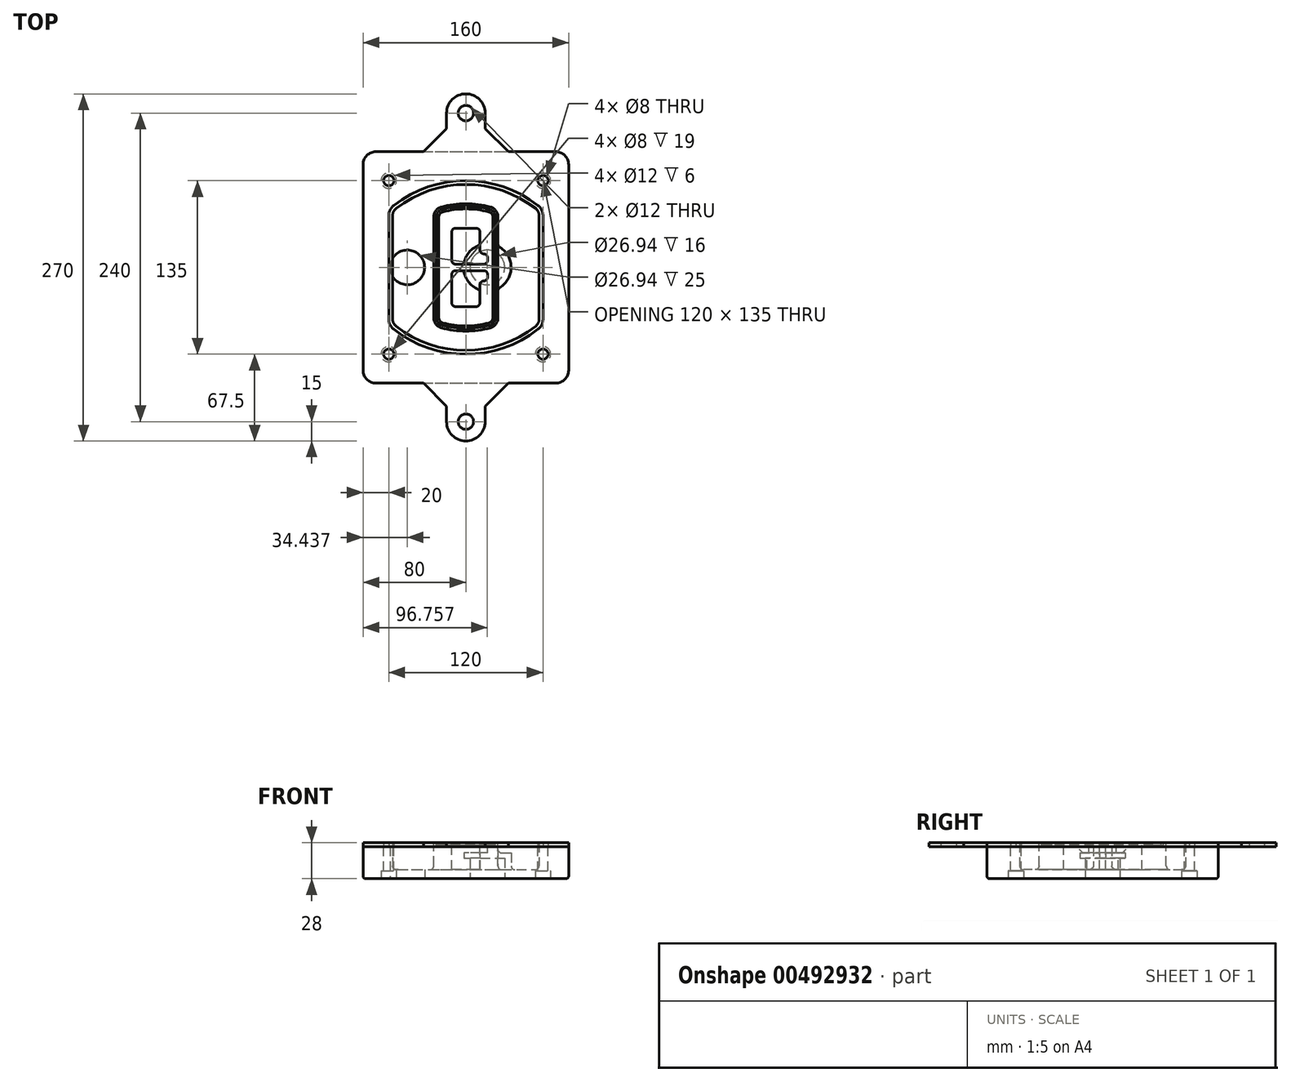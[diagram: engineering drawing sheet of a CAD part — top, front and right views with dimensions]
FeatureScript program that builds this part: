
annotation { "Feature Type Name" : "Feature", "Feature Type Description" : "" }
export const myFeature = defineFeature(function(context is Context, id is Id, definition is map)
    precondition{}
    {
        {
            var Q0;
            Q0=qCreatedBy(makeId("Top.planeOp"),FACE);
            var sketch = newSketch(context, id + "F0", { "sketchPlane" : qUnion([Q0])});
            skPoint(sketch, "E0.rect.middle", {"position": v(0, 0) * mm});
            skLineSegment(sketch, "E1.bottom", {"start": v(-70, -90) * mm, "end": v(70, -90) * mm});
            skLineSegment(sketch, "E1.top", {"start": v(-70, 90) * mm, "end": v(70, 90) * mm});
            skLineSegment(sketch, "E1.left", {"start": v(-80, -80) * mm, "end": v(-80, 80) * mm});
            skLineSegment(sketch, "E1.right", {"start": v(80, -80) * mm, "end": v(80, 80) * mm});
            skLineSegment(sketch, "E2", {"start": v(-80, 90) * mm, "end": v(80, -90) * mm, "construction": true});
            skLineSegment(sketch, "E3", {"start": v(80, 90) * mm, "end": v(-80, -90) * mm, "construction": true});
            skCircle(sketch, "E4", {"center": v(-60, 67.5) * mm, "radius": 4 * mm});
            skCircle(sketch, "E5", {"center": v(60, 67.5) * mm, "radius": 4 * mm});
            skCircle(sketch, "E6", {"center": v(60, -67.5) * mm, "radius": 4 * mm});
            skCircle(sketch, "E7", {"center": v(-60, -67.5) * mm, "radius": 4 * mm});
            skLineSegment(sketch, "E8", {"start": v(-60, 67.5) * mm, "end": v(60, 67.5) * mm, "construction": true});
            skLineSegment(sketch, "E9", {"start": v(60, 67.5) * mm, "end": v(60, -67.5) * mm, "construction": true});
            skLineSegment(sketch, "E10", {"start": v(60, -67.5) * mm, "end": v(-60, -67.5) * mm, "construction": true});
            skLineSegment(sketch, "E11", {"start": v(-60, -67.5) * mm, "end": v(-60, 67.5) * mm, "construction": true});
            skLineSegment(sketch, "E12", {"start": v(-60, 40.3) * mm, "end": v(-60, -40.3) * mm});
            skLineSegment(sketch, "E13", {"start": v(60, 40.3) * mm, "end": v(60, -40.3) * mm});
            skArc(sketch, "E14", {"start": v(56.15, 48.18) * mm, "mid": v(0, 67.5) * mm, "end": v(-56.15, 48.18) * mm});
            skArc(sketch, "E15", {"start": v(-56.15, -48.18) * mm, "mid": v(0, -67.5) * mm, "end": v(56.15, -48.18) * mm});
            skLineSegment(sketch, "E16", {"start": v(-60, 0) * mm, "end": v(60, 0) * mm, "construction": true});
            skPoint(sketch, "E17.visualSharp", {"position": v(-60, -45) * mm});
            skArc(sketch, "E17.filletArc", {"start": v(-60, -40.3) * mm, "mid": v(-58.99, -44.68) * mm, "end": v(-56.15, -48.18) * mm});
            skPoint(sketch, "E18.visualSharp", {"position": v(-60, 45) * mm});
            skArc(sketch, "E18.filletArc", {"start": v(-56.15, 48.18) * mm, "mid": v(-58.99, 44.68) * mm, "end": v(-60, 40.3) * mm});
            skPoint(sketch, "E19.visualSharp", {"position": v(60, 45) * mm});
            skArc(sketch, "E19.filletArc", {"start": v(60, 40.3) * mm, "mid": v(58.99, 44.68) * mm, "end": v(56.15, 48.18) * mm});
            skPoint(sketch, "E20.visualSharp", {"position": v(60, -45) * mm});
            skArc(sketch, "E20.filletArc", {"start": v(56.15, -48.18) * mm, "mid": v(58.99, -44.68) * mm, "end": v(60, -40.3) * mm});
            skPoint(sketch, "E21.visualSharp", {"position": v(-80, 90) * mm});
            skArc(sketch, "E21.filletArc", {"start": v(-70, 90) * mm, "mid": v(-77.07, 87.07) * mm, "end": v(-80, 80) * mm});
            skPoint(sketch, "E22.visualSharp", {"position": v(80, 90) * mm});
            skArc(sketch, "E22.filletArc", {"start": v(80, 80) * mm, "mid": v(77.07, 87.07) * mm, "end": v(70, 90) * mm});
            skPoint(sketch, "E23.visualSharp", {"position": v(80, -90) * mm});
            skArc(sketch, "E23.filletArc", {"start": v(70, -90) * mm, "mid": v(77.07, -87.07) * mm, "end": v(80, -80) * mm});
            skPoint(sketch, "E24.visualSharp", {"position": v(-80, -90) * mm});
            skArc(sketch, "E24.filletArc", {"start": v(-80, -80) * mm, "mid": v(-77.07, -87.07) * mm, "end": v(-70, -90) * mm});
            skArc(sketch, "E25.0", {"start": v(57, 40.3) * mm, "mid": v(56.3, 43.36) * mm, "end": v(54.3, 45.81) * mm});
            skLineSegment(sketch, "E25.1", {"start": v(57, 40.3) * mm, "end": v(57, -40.3) * mm});
            skArc(sketch, "E25.2", {"start": v(54.3, -45.81) * mm, "mid": v(56.3, -43.36) * mm, "end": v(57, -40.3) * mm});
            skArc(sketch, "E25.3", {"start": v(-54.3, -45.81) * mm, "mid": v(0, -64.5) * mm, "end": v(54.3, -45.81) * mm});
            skArc(sketch, "E25.4", {"start": v(-57, -40.3) * mm, "mid": v(-56.3, -43.36) * mm, "end": v(-54.3, -45.81) * mm});
            skArc(sketch, "E25.5", {"start": v(54.3, 45.81) * mm, "mid": v(0, 64.5) * mm, "end": v(-54.3, 45.81) * mm});
            skLineSegment(sketch, "E25.6", {"start": v(-57, 40.3) * mm, "end": v(-57, -40.3) * mm});
            skArc(sketch, "E25.7", {"start": v(-54.3, 45.81) * mm, "mid": v(-56.3, 43.36) * mm, "end": v(-57, 40.3) * mm});
            skArc(sketch, "E26.0", {"start": v(-58.62, 51.33) * mm, "mid": v(-62.58, 46.43) * mm, "end": v(-64, 40.3) * mm});
            skArc(sketch, "E26.1", {"start": v(58.62, 51.33) * mm, "mid": v(0, 71.5) * mm, "end": v(-58.62, 51.33) * mm});
            skArc(sketch, "E26.2", {"start": v(64, 40.3) * mm, "mid": v(62.58, 46.43) * mm, "end": v(58.62, 51.33) * mm});
            skLineSegment(sketch, "E26.3", {"start": v(64, 40.3) * mm, "end": v(64, -40.3) * mm});
            skArc(sketch, "E26.4", {"start": v(58.62, -51.33) * mm, "mid": v(62.58, -46.43) * mm, "end": v(64, -40.3) * mm});
            skLineSegment(sketch, "E26.5", {"start": v(-64, 40.3) * mm, "end": v(-64, -40.3) * mm});
            skArc(sketch, "E26.6", {"start": v(-58.62, -51.33) * mm, "mid": v(0, -71.5) * mm, "end": v(58.62, -51.33) * mm});
            skArc(sketch, "E26.7", {"start": v(-64, -40.3) * mm, "mid": v(-62.58, -46.43) * mm, "end": v(-58.62, -51.33) * mm});
            skSolve(sketch);
        }
        {
            var Q0;
            Q0=makeQuery(id+"F0.imprint","IMPRINT",FACE,{"disambiguationData":[TD([[makeQuery(id+"F0.imprint","IMPRINT",EDGE,{"derivedFrom":sQuery(id+"F0.wireOp",EDGE,"E1.bottom")}),1.0]])]});
            var Q1;
            Q1=makeQuery(id+"F0.imprint","IMPRINT",FACE,{"disambiguationData":[TD([[makeQuery(id+"F0.imprint","IMPRINT",EDGE,{"derivedFrom":sQuery(id+"F0.wireOp",EDGE,"E12")}),1.0]])]});
            var Q2;
            Q2=makeQuery(id+"F0.imprint","IMPRINT",FACE,{"disambiguationData":[TD([[makeQuery(id+"F0.imprint","IMPRINT",EDGE,{"derivedFrom":sQuery(id+"F0.wireOp",EDGE,"E25.0")}),1.0]])]});
            var Q3;
            Q3=makeQuery(id+"F0.imprint","IMPRINT",FACE,{"disambiguationData":[TD([[makeQuery(id+"F0.imprint","IMPRINT",EDGE,{"derivedFrom":sQuery(id+"F0.wireOp",EDGE,"E12")}),-1.0]])]});
            extrude(context, id + "F1", {"entities" : qUnion([Q0, Q1, Q2, Q3]), "oppositeDirection" : true, "depth" : 25 * mm});
        }
        {
            var Q0;
            Q0=makeQuery(id+"F0.imprint","IMPRINT",FACE,{"disambiguationData":[TD([[makeQuery(id+"F0.imprint","IMPRINT",EDGE,{"derivedFrom":sQuery(id+"F0.wireOp",EDGE,"E12")}),1.0]])]});
            extrude(context, id + "F2", {"entities" : qUnion([Q0]), "operationType" : NewBodyOperationType.ADD, "depth" : 3 * mm});
        }
        {
            var Q0;
            Q0=makeQuery(id+"F0.imprint","IMPRINT",FACE,{"disambiguationData":[TD([[makeQuery(id+"F0.imprint","IMPRINT",EDGE,{"derivedFrom":sQuery(id+"F0.wireOp",EDGE,"E25.0")}),1.0]])]});
            extrude(context, id + "F3", {"entities" : qUnion([Q0]), "operationType" : NewBodyOperationType.REMOVE, "oppositeDirection" : true, "depth" : 18 * mm});
        }
        {
            var Q0;
            Q0=makeQuery(id+"F2.opExtrude","CAP_FACE",FACE,{"disambiguationData":[OSD([sQuery(id+"F0.wireOp",EDGE,"E12"),sQuery(id+"F0.wireOp",EDGE,"E13"),sQuery(id+"F0.wireOp",EDGE,"E14"),sQuery(id+"F0.wireOp",EDGE,"E15"),sQuery(id+"F0.wireOp",EDGE,"E17.filletArc"),sQuery(id+"F0.wireOp",EDGE,"E18.filletArc"),sQuery(id+"F0.wireOp",EDGE,"E19.filletArc"),sQuery(id+"F0.wireOp",EDGE,"E20.filletArc"),sQuery(id+"F0.wireOp",EDGE,"E25.0"),sQuery(id+"F0.wireOp",EDGE,"E25.1"),sQuery(id+"F0.wireOp",EDGE,"E25.2"),sQuery(id+"F0.wireOp",EDGE,"E25.3"),sQuery(id+"F0.wireOp",EDGE,"E25.4"),sQuery(id+"F0.wireOp",EDGE,"E25.5"),sQuery(id+"F0.wireOp",EDGE,"E25.6"),sQuery(id+"F0.wireOp",EDGE,"E25.7")])],"isStart":false});
            var sketch = newSketch(context, id + "F4", { "sketchPlane" : qUnion([Q0])});
            skArc(sketch, "E27.0", {"start": v(-19.08, -46.97) * mm, "mid": v(0, -49.5) * mm, "end": v(19.08, -46.97) * mm});
            skArc(sketch, "E28.0", {"start": v(19.08, 46.97) * mm, "mid": v(0, 49.5) * mm, "end": v(-19.08, 46.97) * mm});
            skLineSegment(sketch, "E29", {"start": v(-25, 39.25) * mm, "end": v(-25, -39.25) * mm});
            skLineSegment(sketch, "E30", {"start": v(25, 39.25) * mm, "end": v(25, -39.25) * mm});
            skLineSegment(sketch, "E31", {"start": v(-25, 45.1) * mm, "end": v(25, 45.1) * mm, "construction": true});
            skLineSegment(sketch, "E32", {"start": v(-25, -45.1) * mm, "end": v(25, -45.1) * mm, "construction": true});
            skPoint(sketch, "E33.visualSharp", {"position": v(-25, 45.1) * mm});
            skArc(sketch, "E33.filletArc", {"start": v(-19.08, 46.97) * mm, "mid": v(-23.35, 44.11) * mm, "end": v(-25, 39.25) * mm});
            skPoint(sketch, "E34.visualSharp", {"position": v(25, 45.1) * mm});
            skArc(sketch, "E34.filletArc", {"start": v(25, 39.25) * mm, "mid": v(23.35, 44.11) * mm, "end": v(19.08, 46.97) * mm});
            skPoint(sketch, "E35.visualSharp", {"position": v(25, -45.1) * mm});
            skArc(sketch, "E35.filletArc", {"start": v(19.08, -46.97) * mm, "mid": v(23.35, -44.11) * mm, "end": v(25, -39.25) * mm});
            skPoint(sketch, "E36.visualSharp", {"position": v(-25, -45.1) * mm});
            skArc(sketch, "E36.filletArc", {"start": v(-25, -39.25) * mm, "mid": v(-23.35, -44.11) * mm, "end": v(-19.08, -46.97) * mm});
            skArc(sketch, "E37.0", {"start": v(54.3, 45.81) * mm, "mid": v(0, 64.5) * mm, "end": v(-54.3, 45.81) * mm});
            skArc(sketch, "E37.1", {"start": v(-54.3, 45.81) * mm, "mid": v(-56.3, 43.36) * mm, "end": v(-57, 40.3) * mm});
            skLineSegment(sketch, "E37.2", {"start": v(-57, 40.3) * mm, "end": v(-57, -40.3) * mm});
            skArc(sketch, "E37.3", {"start": v(-57, -40.3) * mm, "mid": v(-56.3, -43.36) * mm, "end": v(-54.3, -45.81) * mm});
            skArc(sketch, "E37.4", {"start": v(-54.3, -45.81) * mm, "mid": v(0, -64.5) * mm, "end": v(54.3, -45.81) * mm});
            skArc(sketch, "E37.5", {"start": v(54.3, -45.81) * mm, "mid": v(56.3, -43.36) * mm, "end": v(57, -40.3) * mm});
            skLineSegment(sketch, "E37.6", {"start": v(57, 40.3) * mm, "end": v(57, -40.3) * mm});
            skArc(sketch, "E37.7", {"start": v(57, 40.3) * mm, "mid": v(56.3, 43.36) * mm, "end": v(54.3, 45.81) * mm});
            skLineSegment(sketch, "E38.0", {"start": v(23, 39.25) * mm, "end": v(23, -39.25) * mm});
            skArc(sketch, "E38.1", {"start": v(18.56, -45.04) * mm, "mid": v(21.76, -42.9) * mm, "end": v(23, -39.25) * mm});
            skArc(sketch, "E38.2", {"start": v(-18.56, -45.04) * mm, "mid": v(0, -47.5) * mm, "end": v(18.56, -45.04) * mm});
            skArc(sketch, "E38.3", {"start": v(-23, -39.25) * mm, "mid": v(-21.76, -42.9) * mm, "end": v(-18.56, -45.04) * mm});
            skLineSegment(sketch, "E38.4", {"start": v(-23, 39.25) * mm, "end": v(-23, -39.25) * mm});
            skArc(sketch, "E38.5", {"start": v(23, 39.25) * mm, "mid": v(21.76, 42.9) * mm, "end": v(18.56, 45.04) * mm});
            skArc(sketch, "E38.6", {"start": v(-18.56, 45.04) * mm, "mid": v(-21.76, 42.9) * mm, "end": v(-23, 39.25) * mm});
            skArc(sketch, "E38.7", {"start": v(18.56, 45.04) * mm, "mid": v(0, 47.5) * mm, "end": v(-18.56, 45.04) * mm});
            skArc(sketch, "E39.0", {"start": v(21, 39.25) * mm, "mid": v(20.18, 41.68) * mm, "end": v(18.04, 43.1) * mm});
            skLineSegment(sketch, "E39.1", {"start": v(21, 39.25) * mm, "end": v(21, -39.25) * mm});
            skArc(sketch, "E39.2", {"start": v(18.04, -43.1) * mm, "mid": v(20.18, -41.68) * mm, "end": v(21, -39.25) * mm});
            skArc(sketch, "E39.3", {"start": v(-18.04, -43.1) * mm, "mid": v(0, -45.5) * mm, "end": v(18.04, -43.1) * mm});
            skArc(sketch, "E39.4", {"start": v(-21, -39.25) * mm, "mid": v(-20.18, -41.68) * mm, "end": v(-18.04, -43.1) * mm});
            skArc(sketch, "E39.5", {"start": v(18.04, 43.1) * mm, "mid": v(0, 45.5) * mm, "end": v(-18.04, 43.1) * mm});
            skLineSegment(sketch, "E39.6", {"start": v(-21, 39.25) * mm, "end": v(-21, -39.25) * mm});
            skArc(sketch, "E39.7", {"start": v(-18.04, 43.1) * mm, "mid": v(-20.18, 41.68) * mm, "end": v(-21, 39.25) * mm});
            skLineSegment(sketch, "E40", {"start": v(-25, 0) * mm, "end": v(25, 0) * mm, "construction": true});
            skLineSegment(sketch, "E41", {"start": v(-11, 5.5) * mm, "end": v(-11, 27.5) * mm});
            skLineSegment(sketch, "E42", {"start": v(-8, 30.5) * mm, "end": v(8, 30.5) * mm});
            skLineSegment(sketch, "E43", {"start": v(11, 27.5) * mm, "end": v(11, 13.5) * mm});
            skLineSegment(sketch, "E44", {"start": v(14, 10.5) * mm, "end": v(14, 10.5) * mm});
            skLineSegment(sketch, "E45", {"start": v(17, 7.5) * mm, "end": v(17, 5.5) * mm});
            skLineSegment(sketch, "E46", {"start": v(14, 2.5) * mm, "end": v(-8, 2.5) * mm});
            skPoint(sketch, "E47.visualSharp", {"position": v(-11, 30.5) * mm});
            skArc(sketch, "E47.filletArc", {"start": v(-8, 30.5) * mm, "mid": v(-10.12, 29.62) * mm, "end": v(-11, 27.5) * mm});
            skPoint(sketch, "E48.visualSharp", {"position": v(11, 30.5) * mm});
            skArc(sketch, "E48.filletArc", {"start": v(11, 27.5) * mm, "mid": v(10.12, 29.62) * mm, "end": v(8, 30.5) * mm});
            skPoint(sketch, "E49.visualSharp", {"position": v(11, 10.5) * mm});
            skArc(sketch, "E49.filletArc", {"start": v(11, 13.5) * mm, "mid": v(11.88, 11.38) * mm, "end": v(14, 10.5) * mm});
            skPoint(sketch, "E50.visualSharp", {"position": v(17, 10.5) * mm});
            skArc(sketch, "E50.filletArc", {"start": v(17, 7.5) * mm, "mid": v(16.12, 9.62) * mm, "end": v(14, 10.5) * mm});
            skPoint(sketch, "E51.visualSharp", {"position": v(17, 2.5) * mm});
            skArc(sketch, "E51.filletArc", {"start": v(14, 2.5) * mm, "mid": v(16.12, 3.38) * mm, "end": v(17, 5.5) * mm});
            skPoint(sketch, "E52.visualSharp", {"position": v(-11, 2.5) * mm});
            skArc(sketch, "E52.filletArc", {"start": v(-11, 5.5) * mm, "mid": v(-10.12, 3.38) * mm, "end": v(-8, 2.5) * mm});
            skLineSegment(sketch, "E53.0.MirrorCS", {"start": v(14, -2.5) * mm, "end": v(-8, -2.5) * mm});
            skArc(sketch, "E54.0.MirrorCS", {"start": v(-11, -5.5) * mm, "mid": v(-10.12, -3.38) * mm, "end": v(-8, -2.5) * mm});
            skLineSegment(sketch, "E55.0.MirrorCS", {"start": v(-11, -5.5) * mm, "end": v(-11, -27.5) * mm});
            skArc(sketch, "E56.0.MirrorCS", {"start": v(-8, -30.5) * mm, "mid": v(-10.12, -29.62) * mm, "end": v(-11, -27.5) * mm});
            skLineSegment(sketch, "E57.0.MirrorCS", {"start": v(-8, -30.5) * mm, "end": v(8, -30.5) * mm});
            skArc(sketch, "E58.0.MirrorCS", {"start": v(11, -27.5) * mm, "mid": v(10.12, -29.62) * mm, "end": v(8, -30.5) * mm});
            skLineSegment(sketch, "E59.0.MirrorCS", {"start": v(11, -27.5) * mm, "end": v(11, -13.5) * mm});
            skArc(sketch, "E60.0.MirrorCS", {"start": v(11, -13.5) * mm, "mid": v(11.88, -11.38) * mm, "end": v(14, -10.5) * mm});
            skArc(sketch, "E61.0.MirrorCS", {"start": v(17, -7.5) * mm, "mid": v(16.12, -9.62) * mm, "end": v(14, -10.5) * mm});
            skLineSegment(sketch, "E62.0.MirrorCS", {"start": v(17, -7.5) * mm, "end": v(17, -5.5) * mm});
            skArc(sketch, "E63.0.MirrorCS", {"start": v(14, -2.5) * mm, "mid": v(16.12, -3.38) * mm, "end": v(17, -5.5) * mm});
            skSolve(sketch);
        }
        {
            var Q0;
            Q0=makeQuery(id+"F4.imprint","IMPRINT",FACE,{"disambiguationData":[TD([[makeQuery(id+"F4.imprint","IMPRINT",EDGE,{"derivedFrom":sQuery(id+"F4.wireOp",EDGE,"E27.0")}),1.0]])]});
            var Q1;
            Q1=makeQuery(id+"F4.imprint","IMPRINT",FACE,{"disambiguationData":[TD([[makeQuery(id+"F4.imprint","IMPRINT",EDGE,{"derivedFrom":sQuery(id+"F4.wireOp",EDGE,"E38.0")}),-1.0]])]});
            var Q2;
            Q2=makeQuery(id+"F4.imprint","IMPRINT",FACE,{"disambiguationData":[TD([[makeQuery(id+"F4.imprint","IMPRINT",EDGE,{"derivedFrom":sQuery(id+"F4.wireOp",EDGE,"E39.0")}),1.0]])]});
            extrude(context, id + "F5", {"entities" : qUnion([Q0, Q1, Q2]), "operationType" : NewBodyOperationType.ADD, "endBound" : BoundingType.UP_TO_NEXT, "oppositeDirection" : true, "depth" : 25 * mm});
        }
        {
            var Q0;
            Q0=makeQuery(id+"F4.imprint","IMPRINT",FACE,{"disambiguationData":[TD([[makeQuery(id+"F4.imprint","IMPRINT",EDGE,{"derivedFrom":sQuery(id+"F4.wireOp",EDGE,"E38.0")}),-1.0]])]});
            extrude(context, id + "F6", {"entities" : qUnion([Q0]), "operationType" : NewBodyOperationType.REMOVE, "oppositeDirection" : true, "depth" : 2 * mm});
        }
        {
            var Q0;
            Q0=makeQuery(id+"F1.opExtrude","CAP_FACE",FACE,{"disambiguationData":[OSD([sQuery(id+"F0.wireOp",EDGE,"E1.bottom"),sQuery(id+"F0.wireOp",EDGE,"E1.top"),sQuery(id+"F0.wireOp",EDGE,"E1.left"),sQuery(id+"F0.wireOp",EDGE,"E1.right"),sQuery(id+"F0.wireOp",EDGE,"E4"),sQuery(id+"F0.wireOp",EDGE,"E5"),sQuery(id+"F0.wireOp",EDGE,"E6"),sQuery(id+"F0.wireOp",EDGE,"E7"),sQuery(id+"F0.wireOp",EDGE,"E21.filletArc"),sQuery(id+"F0.wireOp",EDGE,"E22.filletArc"),sQuery(id+"F0.wireOp",EDGE,"E23.filletArc"),sQuery(id+"F0.wireOp",EDGE,"E24.filletArc")])],"isStart":false});
            var sketch = newSketch(context, id + "F7", { "sketchPlane" : qUnion([Q0])});
            skCircle(sketch, "E64", {"center": v(16.76, 0) * mm, "radius": 13.47 * mm});
            skCircle(sketch, "E65", {"center": v(-45.56, 0) * mm, "radius": 13.47 * mm});
            skLineSegment(sketch, "E66", {"start": v(80, 0) * mm, "end": v(-80, 0) * mm});
            skCircle(sketch, "E67", {"center": v(16.76, 0) * mm, "radius": 18.47 * mm});
            skCircle(sketch, "E68", {"center": v(60, -67.5) * mm, "radius": 6 * mm});
            skCircle(sketch, "E69", {"center": v(-60, -67.5) * mm, "radius": 6 * mm});
            skCircle(sketch, "E70", {"center": v(-60, 67.5) * mm, "radius": 6 * mm});
            skCircle(sketch, "E71", {"center": v(60, 67.5) * mm, "radius": 6 * mm});
            skSolve(sketch);
        }
        {
            var Q0;
            {var subQ1=sQuery(id+"F7.wireOp",EDGE,"E66");var subQ4=sQuery(id+"F7.wireOp",EDGE,"E64");var subQ6=makeQuery(id+"F7.imprint","INTERSECT",VERTEX,{"disambiguationData":[OD(0.0)],"derivedFrom":[subQ4,subQ1]});Q0=makeQuery(id+"F7.imprint","IMPRINT",FACE,{"disambiguationData":[TD([[makeQuery(id+"F7.imprint","IMPRINT",EDGE,{"disambiguationData":[TD([[subQ6,-1.0]])],"derivedFrom":subQ4}),-1.0]])]});}
            var Q1;
            {var subQ0=sQuery(id+"F7.wireOp",EDGE,"E66");var subQ1=sQuery(id+"F7.wireOp",EDGE,"E64");var subQ3=makeQuery(id+"F7.imprint","INTERSECT",VERTEX,{"disambiguationData":[OD(0.0)],"derivedFrom":[subQ1,subQ0]});Q1=makeQuery(id+"F7.imprint","IMPRINT",FACE,{"disambiguationData":[TD([[makeQuery(id+"F7.imprint","IMPRINT",EDGE,{"disambiguationData":[TD([[subQ3,-1.0]])],"derivedFrom":subQ1}),1.0]])]});}
            var Q2;
            {var subQ0=sQuery(id+"F7.wireOp",EDGE,"E66");var subQ1=sQuery(id+"F7.wireOp",EDGE,"E64");var subQ3=makeQuery(id+"F7.imprint","INTERSECT",VERTEX,{"disambiguationData":[OD(0.0)],"derivedFrom":[subQ1,subQ0]});Q2=makeQuery(id+"F7.imprint","IMPRINT",FACE,{"disambiguationData":[TD([[makeQuery(id+"F7.imprint","IMPRINT",EDGE,{"disambiguationData":[TD([[subQ3,1.0]])],"derivedFrom":subQ1}),1.0]])]});}
            var Q3;
            {var subQ1=sQuery(id+"F7.wireOp",EDGE,"E66");var subQ4=sQuery(id+"F7.wireOp",EDGE,"E64");var subQ6=makeQuery(id+"F7.imprint","INTERSECT",VERTEX,{"disambiguationData":[OD(0.0)],"derivedFrom":[subQ4,subQ1]});Q3=makeQuery(id+"F7.imprint","IMPRINT",FACE,{"disambiguationData":[TD([[makeQuery(id+"F7.imprint","IMPRINT",EDGE,{"disambiguationData":[TD([[subQ6,1.0]])],"derivedFrom":subQ4}),-1.0]])]});}
            extrude(context, id + "F8", {"entities" : qUnion([Q0, Q1, Q2, Q3]), "operationType" : NewBodyOperationType.ADD, "oppositeDirection" : true, "depth" : 20 * mm});
        }
        {
            var Q0;
            {var subQ0=sQuery(id+"F7.wireOp",EDGE,"E66");var subQ1=sQuery(id+"F7.wireOp",EDGE,"E64");var subQ3=makeQuery(id+"F7.imprint","INTERSECT",VERTEX,{"disambiguationData":[OD(0.0)],"derivedFrom":[subQ1,subQ0]});Q0=makeQuery(id+"F7.imprint","IMPRINT",FACE,{"disambiguationData":[TD([[makeQuery(id+"F7.imprint","IMPRINT",EDGE,{"disambiguationData":[TD([[subQ3,-1.0]])],"derivedFrom":subQ1}),1.0]])]});}
            var Q1;
            {var subQ0=sQuery(id+"F7.wireOp",EDGE,"E66");var subQ1=sQuery(id+"F7.wireOp",EDGE,"E64");var subQ3=makeQuery(id+"F7.imprint","INTERSECT",VERTEX,{"disambiguationData":[OD(0.0)],"derivedFrom":[subQ1,subQ0]});Q1=makeQuery(id+"F7.imprint","IMPRINT",FACE,{"disambiguationData":[TD([[makeQuery(id+"F7.imprint","IMPRINT",EDGE,{"disambiguationData":[TD([[subQ3,1.0]])],"derivedFrom":subQ1}),1.0]])]});}
            extrude(context, id + "F9", {"entities" : qUnion([Q0, Q1]), "operationType" : NewBodyOperationType.REMOVE, "oppositeDirection" : true, "depth" : 16 * mm});
        }
        {
            var Q0;
            {var subQ0=sQuery(id+"F7.wireOp",EDGE,"E66");var subQ1=sQuery(id+"F7.wireOp",EDGE,"E65");var subQ3=makeQuery(id+"F7.imprint","INTERSECT",VERTEX,{"disambiguationData":[OD(0.0)],"derivedFrom":[subQ1,subQ0]});Q0=makeQuery(id+"F7.imprint","IMPRINT",FACE,{"disambiguationData":[TD([[makeQuery(id+"F7.imprint","IMPRINT",EDGE,{"disambiguationData":[TD([[subQ3,-1.0]])],"derivedFrom":subQ1}),1.0]])]});}
            var Q1;
            {var subQ0=sQuery(id+"F7.wireOp",EDGE,"E66");var subQ1=sQuery(id+"F7.wireOp",EDGE,"E65");var subQ3=makeQuery(id+"F7.imprint","INTERSECT",VERTEX,{"disambiguationData":[OD(0.0)],"derivedFrom":[subQ1,subQ0]});Q1=makeQuery(id+"F7.imprint","IMPRINT",FACE,{"disambiguationData":[TD([[makeQuery(id+"F7.imprint","IMPRINT",EDGE,{"disambiguationData":[TD([[subQ3,1.0]])],"derivedFrom":subQ1}),1.0]])]});}
            extrude(context, id + "F10", {"entities" : qUnion([Q0, Q1]), "operationType" : NewBodyOperationType.REMOVE, "oppositeDirection" : true, "depth" : 25 * mm});
        }
        {
            var Q0;
            Q0=makeQuery(id+"F7.imprint","IMPRINT",FACE,{"disambiguationData":[TD([[makeQuery(id+"F7.imprint","IMPRINT",EDGE,{"derivedFrom":sQuery(id+"F7.wireOp",EDGE,"E68")}),1.0]])]});
            var Q1;
            Q1=makeQuery(id+"F7.imprint","IMPRINT",FACE,{"disambiguationData":[TD([[makeQuery(id+"F7.imprint","IMPRINT",EDGE,{"derivedFrom":makeQuery(id+"F1.opExtrude","CAP_EDGE",EDGE,{"disambiguationData":[OSD([sQuery(id+"F0.wireOp",EDGE,"E5")])],"isStart":false})}),-1.0]])]});
            var Q2;
            Q2=makeQuery(id+"F7.imprint","IMPRINT",FACE,{"disambiguationData":[TD([[makeQuery(id+"F7.imprint","IMPRINT",EDGE,{"derivedFrom":sQuery(id+"F7.wireOp",EDGE,"E69")}),1.0]])]});
            var Q3;
            Q3=makeQuery(id+"F7.imprint","IMPRINT",FACE,{"disambiguationData":[TD([[makeQuery(id+"F7.imprint","IMPRINT",EDGE,{"derivedFrom":makeQuery(id+"F1.opExtrude","CAP_EDGE",EDGE,{"disambiguationData":[OSD([sQuery(id+"F0.wireOp",EDGE,"E4")])],"isStart":false})}),-1.0]])]});
            var Q4;
            Q4=makeQuery(id+"F7.imprint","IMPRINT",FACE,{"disambiguationData":[TD([[makeQuery(id+"F7.imprint","IMPRINT",EDGE,{"derivedFrom":sQuery(id+"F7.wireOp",EDGE,"E70")}),1.0]])]});
            var Q5;
            Q5=makeQuery(id+"F7.imprint","IMPRINT",FACE,{"disambiguationData":[TD([[makeQuery(id+"F7.imprint","IMPRINT",EDGE,{"derivedFrom":makeQuery(id+"F1.opExtrude","CAP_EDGE",EDGE,{"disambiguationData":[OSD([sQuery(id+"F0.wireOp",EDGE,"E7")])],"isStart":false})}),-1.0]])]});
            var Q6;
            Q6=makeQuery(id+"F7.imprint","IMPRINT",FACE,{"disambiguationData":[TD([[makeQuery(id+"F7.imprint","IMPRINT",EDGE,{"derivedFrom":sQuery(id+"F7.wireOp",EDGE,"E71")}),1.0]])]});
            var Q7;
            Q7=makeQuery(id+"F7.imprint","IMPRINT",FACE,{"disambiguationData":[TD([[makeQuery(id+"F7.imprint","IMPRINT",EDGE,{"derivedFrom":makeQuery(id+"F1.opExtrude","CAP_EDGE",EDGE,{"disambiguationData":[OSD([sQuery(id+"F0.wireOp",EDGE,"E6")])],"isStart":false})}),-1.0]])]});
            extrude(context, id + "F11", {"entities" : qUnion([Q0, Q1, Q2, Q3, Q4, Q5, Q6, Q7]), "operationType" : NewBodyOperationType.REMOVE, "oppositeDirection" : true, "depth" : 6 * mm});
        }
        {
            var Q0;
            Q0=makeQuery(id+"F9.boolean.opBoolean","COPY",FACE,{"derivedFrom":makeQuery(id+"F9.opExtrude","CAP_FACE",FACE,{"disambiguationData":[OSD([sQuery(id+"F7.wireOp",EDGE,"E64")])],"isStart":false})});
            var sketch = newSketch(context, id + "F12", { "sketchPlane" : qUnion([Q0])});
            skArc(sketch, "E72.0", {"start": v(11, 17.55) * mm, "mid": v(2.57, 11.82) * mm, "end": v(-1.54, 2.5) * mm});
            skArc(sketch, "E72.1", {"start": v(-1.54, -2.5) * mm, "mid": v(2.57, -11.82) * mm, "end": v(11, -17.55) * mm});
            skLineSegment(sketch, "E73", {"start": v(-1.54, -2.5) * mm, "end": v(14, -2.5) * mm});
            skLineSegment(sketch, "E74.0", {"start": v(14, 2.5) * mm, "end": v(-1.54, 2.5) * mm});
            skArc(sketch, "E74.1", {"start": v(14, 2.5) * mm, "mid": v(16.12, 3.38) * mm, "end": v(17, 5.5) * mm});
            skLineSegment(sketch, "E74.2", {"start": v(17, 7.5) * mm, "end": v(17, 5.5) * mm});
            skArc(sketch, "E74.3", {"start": v(17, 7.5) * mm, "mid": v(16.12, 9.62) * mm, "end": v(14, 10.5) * mm});
            skArc(sketch, "E74.4", {"start": v(11, 13.5) * mm, "mid": v(11.88, 11.38) * mm, "end": v(14, 10.5) * mm});
            skLineSegment(sketch, "E74.5", {"start": v(11, 17.55) * mm, "end": v(11, 13.5) * mm});
            skLineSegment(sketch, "E74.7", {"start": v(14, -2.5) * mm, "end": v(-1.54, -2.5) * mm});
            skArc(sketch, "E74.8", {"start": v(14, -2.5) * mm, "mid": v(16.12, -3.38) * mm, "end": v(17, -5.5) * mm});
            skLineSegment(sketch, "E74.9", {"start": v(17, -7.5) * mm, "end": v(17, -5.5) * mm});
            skArc(sketch, "E74.10", {"start": v(17, -7.5) * mm, "mid": v(16.12, -9.62) * mm, "end": v(14, -10.5) * mm});
            skArc(sketch, "E74.11", {"start": v(11, -13.5) * mm, "mid": v(11.88, -11.38) * mm, "end": v(14, -10.5) * mm});
            skLineSegment(sketch, "E74.12", {"start": v(11, -17.55) * mm, "end": v(11, -13.5) * mm});
            skPoint(sketch, "E75.orphan", {"position": v(11, -27.5) * mm});
            skPoint(sketch, "E76.orphan", {"position": v(-8, -2.5) * mm});
            skPoint(sketch, "E77.orphan", {"position": v(-8, 2.5) * mm});
            skPoint(sketch, "E78.orphan", {"position": v(11, 27.5) * mm});
            skSolve(sketch);
        }
        {
            var Q0;
            {var subQ7=sQuery(id+"F12.wireOp",EDGE,"E72.0");var subQ14=sQuery(id+"F12.wireOp",EDGE,"E72.1");var subQ16=sQuery(id+"F12.wireOp",EDGE,"E74.1");var subQ18=sQuery(id+"F12.wireOp",EDGE,"E74.8");Q0=qUnion([makeQuery(id+"F12.imprint","IMPRINT",FACE,{"disambiguationData":[TD([[makeQuery(id+"F12.imprint","IMPRINT",EDGE,{"derivedFrom":subQ7}),1.0]])]}),makeQuery(id+"F12.imprint","IMPRINT",FACE,{"disambiguationData":[TD([[makeQuery(id+"F12.imprint","IMPRINT",EDGE,{"derivedFrom":subQ14}),1.0]])]}),makeQuery(id+"F12.imprint","IMPRINT",FACE,{"disambiguationData":[TD([[makeQuery(id+"F12.imprint","IMPRINT",EDGE,{"derivedFrom":subQ16}),1.0]])]}),makeQuery(id+"F12.imprint","IMPRINT",FACE,{"disambiguationData":[TD([[makeQuery(id+"F12.imprint","IMPRINT",EDGE,{"derivedFrom":subQ18}),-1.0]])]})]);}
            var Q1;
            Q1=makeQuery(id+"F5.boolean.opBoolean","SPLIT",FACE,{"disambiguationData":[TD([makeQuery(id+"F5.opExtrude","SWEPT_FACE",FACE,{"disambiguationData":[OSD([sQuery(id+"F4.wireOp",EDGE,"E41")])]})])],"derivedFrom":makeQuery(id+"F3.boolean.opBoolean","COPY",FACE,{"derivedFrom":makeQuery(id+"F3.opExtrude","CAP_FACE",FACE,{"disambiguationData":[OSD([sQuery(id+"F0.wireOp",EDGE,"E25.0"),sQuery(id+"F0.wireOp",EDGE,"E25.1"),sQuery(id+"F0.wireOp",EDGE,"E25.2"),sQuery(id+"F0.wireOp",EDGE,"E25.3"),sQuery(id+"F0.wireOp",EDGE,"E25.4"),sQuery(id+"F0.wireOp",EDGE,"E25.5"),sQuery(id+"F0.wireOp",EDGE,"E25.6"),sQuery(id+"F0.wireOp",EDGE,"E25.7")])],"isStart":false})})});
            extrude(context, id + "F13", {"entities" : qUnion([Q0]), "operationType" : NewBodyOperationType.REMOVE, "endBound" : BoundingType.UP_TO_SURFACE, "endBoundEntityFace" : qUnion([Q1]), "depth" : 25 * mm});
        }
        {
            var Q0;
            Q0=makeQuery(id+"F3.boolean.opBoolean","COPY",EDGE,{"derivedFrom":makeQuery(id+"F3.opExtrude","CAP_EDGE",EDGE,{"disambiguationData":[OSD([sQuery(id+"F0.wireOp",EDGE,"E25.6")])],"isStart":false})});
            var Q1;
            Q1=makeQuery(id+"F8.boolean.opBoolean","INTERSECT",EDGE,{"derivedFrom":[makeQuery(id+"F5.opExtrude","SWEPT_FACE",FACE,{"disambiguationData":[OSD([sQuery(id+"F4.wireOp",EDGE,"E30")])]}),makeQuery(id+"F8.opExtrude","CAP_FACE",FACE,{"disambiguationData":[OSD([sQuery(id+"F7.wireOp",EDGE,"E67")])],"isStart":false})]});
            var Q2;
            Q2=makeQuery(id+"F8.boolean.opBoolean","INTERSECT",EDGE,{"disambiguationData":[OD(1.0)],"derivedFrom":[makeQuery(id+"F5.opExtrude","SWEPT_FACE",FACE,{"disambiguationData":[OSD([sQuery(id+"F4.wireOp",EDGE,"E30")])]}),makeQuery(id+"F8.opExtrude","SWEPT_FACE",FACE,{"disambiguationData":[OSD([sQuery(id+"F7.wireOp",EDGE,"E67")])]})]});
            var Q3;
            {var subQ0=sQuery(id+"F4.wireOp",EDGE,"E30");Q3=makeQuery(id+"F8.boolean.opBoolean","SPLIT",EDGE,{"disambiguationData":[TD([makeQuery(id+"F5.opExtrude","SWEPT_FACE",FACE,{"disambiguationData":[OSD([sQuery(id+"F4.wireOp",EDGE,"E35.filletArc")])]})])],"derivedFrom":makeQuery(id+"F5.opExtrude","CAP_EDGE",EDGE,{"disambiguationData":[OSD([subQ0])],"isStart":false})});}
            var Q4;
            {var subQ0=sQuery(id+"F0.wireOp",EDGE,"E25.7");var subQ1=sQuery(id+"F0.wireOp",EDGE,"E25.1");var subQ2=sQuery(id+"F0.wireOp",EDGE,"E25.6");var subQ3=sQuery(id+"F0.wireOp",EDGE,"E25.5");var subQ4=sQuery(id+"F0.wireOp",EDGE,"E25.4");var subQ5=sQuery(id+"F0.wireOp",EDGE,"E25.0");var subQ6=sQuery(id+"F0.wireOp",EDGE,"E25.2");var subQ7=sQuery(id+"F0.wireOp",EDGE,"E25.3");Q4=makeQuery(id+"F8.boolean.opBoolean","INTERSECT",EDGE,{"derivedFrom":[makeQuery(id+"F5.boolean.opBoolean","SPLIT",FACE,{"disambiguationData":[TD([makeQuery(id+"F2.opExtrude","SWEPT_FACE",FACE,{"disambiguationData":[OSD([subQ5])]})])],"derivedFrom":makeQuery(id+"F3.boolean.opBoolean","COPY",FACE,{"derivedFrom":makeQuery(id+"F3.opExtrude","CAP_FACE",FACE,{"disambiguationData":[OSD([subQ5,subQ1,subQ6,subQ7,subQ4,subQ3,subQ2,subQ0])],"isStart":false})})}),makeQuery(id+"F8.opExtrude","SWEPT_FACE",FACE,{"disambiguationData":[OSD([sQuery(id+"F7.wireOp",EDGE,"E67")])]})]});}
            var Q5;
            Q5=makeQuery(id+"F8.boolean.opBoolean","INTERSECT",EDGE,{"disambiguationData":[OD(0.0)],"derivedFrom":[makeQuery(id+"F5.opExtrude","SWEPT_FACE",FACE,{"disambiguationData":[OSD([sQuery(id+"F4.wireOp",EDGE,"E30")])]}),makeQuery(id+"F8.opExtrude","SWEPT_FACE",FACE,{"disambiguationData":[OSD([sQuery(id+"F7.wireOp",EDGE,"E67")])]})]});
            fillet(context, id + "F14", {"entities" : qUnion([Q0, Q1, Q2, Q3, Q4, Q5]), "radius" : 3 * mm, "tangentPropagation" : true, "allowEdgeOverflow" : false});
        }
        {
            var Q0;
            Q0=makeQuery(id+"F1.opExtrude","CAP_EDGE",EDGE,{"disambiguationData":[OSD([sQuery(id+"F0.wireOp",EDGE,"E1.bottom")])],"isStart":false});
            fillet(context, id + "F15", {"entities" : qUnion([Q0]), "radius" : 2 * mm, "tangentPropagation" : true, "allowEdgeOverflow" : false});
        }
        {
            var Q0;
            {var subQ0=sQuery(id+"F0.wireOp",EDGE,"E21.filletArc");var subQ1=sQuery(id+"F0.wireOp",EDGE,"E7");var subQ2=sQuery(id+"F0.wireOp",EDGE,"E6");var subQ3=sQuery(id+"F0.wireOp",EDGE,"E5");var subQ4=sQuery(id+"F0.wireOp",EDGE,"E4");var subQ5=sQuery(id+"F0.wireOp",EDGE,"E22.filletArc");var subQ6=sQuery(id+"F0.wireOp",EDGE,"E1.bottom");var subQ7=sQuery(id+"F0.wireOp",EDGE,"E1.right");var subQ8=sQuery(id+"F0.wireOp",EDGE,"E1.top");var subQ9=sQuery(id+"F0.wireOp",EDGE,"E1.left");var subQ10=sQuery(id+"F0.wireOp",EDGE,"E23.filletArc");var subQ11=sQuery(id+"F0.wireOp",EDGE,"E24.filletArc");Q0=makeQuery(id+"F2.boolean.opBoolean","SPLIT",FACE,{"disambiguationData":[TD([makeQuery(id+"F1.opExtrude","SWEPT_FACE",FACE,{"disambiguationData":[OSD([subQ6])]})])],"derivedFrom":makeQuery(id+"F1.opExtrude","CAP_FACE",FACE,{"disambiguationData":[OSD([subQ6,subQ8,subQ9,subQ7,subQ4,subQ3,subQ2,subQ1,subQ0,subQ5,subQ10,subQ11])],"isStart":true})});}
            var sketch = newSketch(context, id + "F16", { "sketchPlane" : qUnion([Q0])});
            skLineSegment(sketch, "E79", {"start": v(0, 90) * mm, "end": v(0, 120) * mm, "construction": true});
            skCircle(sketch, "E80", {"center": v(0, 120) * mm, "radius": 6 * mm});
            skLineSegment(sketch, "E81", {"start": v(-33, 90) * mm, "end": v(-15, 108) * mm});
            skLineSegment(sketch, "E82", {"start": v(33, 90) * mm, "end": v(15, 108) * mm});
            skArc(sketch, "E83", {"start": v(15, 120) * mm, "mid": v(0, 135) * mm, "end": v(-15, 120) * mm});
            skLineSegment(sketch, "E84", {"start": v(80, 0) * mm, "end": v(-80, 0) * mm, "construction": true});
            skArc(sketch, "E85.MirrorCS", {"start": v(15, -120) * mm, "mid": v(0, -135) * mm, "end": v(-15, -120) * mm});
            skCircle(sketch, "E86.MirrorC", {"center": v(0, -120) * mm, "radius": 6 * mm});
            skLineSegment(sketch, "E87.MirrorCS", {"start": v(0, -90) * mm, "end": v(0, -120) * mm, "construction": true});
            skLineSegment(sketch, "E88.MirrorCS", {"start": v(33, -90) * mm, "end": v(15, -108) * mm});
            skLineSegment(sketch, "E89.MirrorCS", {"start": v(-33, -90) * mm, "end": v(-15, -108) * mm});
            skLineSegment(sketch, "E90", {"start": v(-15, 108) * mm, "end": v(-15, 120) * mm});
            skLineSegment(sketch, "E91", {"start": v(15, 108) * mm, "end": v(15, 120) * mm});
            skLineSegment(sketch, "E92.MirrorCS", {"start": v(15, -108) * mm, "end": v(15, -120) * mm});
            skLineSegment(sketch, "E93.MirrorCS", {"start": v(-15, -108) * mm, "end": v(-15, -120) * mm});
            skSolve(sketch);
        }
        {
            var Q0;
            Q0=makeQuery(id+"F16.imprint","IMPRINT",FACE,{"disambiguationData":[TD([[makeQuery(id+"F16.imprint","IMPRINT",EDGE,{"derivedFrom":sQuery(id+"F16.wireOp",EDGE,"66269ca2-fd63-4bb4-8753-f1fec9d0879a0.MirrorCS")}),1.0]])]});
            var Q1;
            Q1=makeQuery(id+"F16.imprint","IMPRINT",FACE,{"disambiguationData":[TD([[makeQuery(id+"F16.imprint","IMPRINT",EDGE,{"derivedFrom":sQuery(id+"F16.wireOp",EDGE,"E80")}),-1.0]])]});
            var Q2;
            {var subQ1=sQuery(id+"F16.wireOp",EDGE,"E89.MirrorCS");Q2=makeQuery(id+"F16.imprint","IMPRINT",FACE,{"disambiguationData":[TD([[makeQuery(id+"F16.imprint","IMPRINT",EDGE,{"derivedFrom":subQ1}),1.0]])]});}
            var Q3;
            Q3=makeQuery(id+"F16.imprint","IMPRINT",FACE,{"disambiguationData":[TD([[makeQuery(id+"F16.imprint","IMPRINT",EDGE,{"derivedFrom":makeQuery(id+"F1.opExtrude","CAP_EDGE",EDGE,{"disambiguationData":[OSD([sQuery(id+"F0.wireOp",EDGE,"E1.left")])],"isStart":true})}),-1.0]])]});
            var Q4;
            Q4=makeQuery(id+"F2.opExtrude","CAP_FACE",FACE,{"disambiguationData":[OSD([sQuery(id+"F0.wireOp",EDGE,"E12"),sQuery(id+"F0.wireOp",EDGE,"E13"),sQuery(id+"F0.wireOp",EDGE,"E14"),sQuery(id+"F0.wireOp",EDGE,"E15"),sQuery(id+"F0.wireOp",EDGE,"E17.filletArc"),sQuery(id+"F0.wireOp",EDGE,"E18.filletArc"),sQuery(id+"F0.wireOp",EDGE,"E19.filletArc"),sQuery(id+"F0.wireOp",EDGE,"E20.filletArc"),sQuery(id+"F0.wireOp",EDGE,"E25.0"),sQuery(id+"F0.wireOp",EDGE,"E25.1"),sQuery(id+"F0.wireOp",EDGE,"E25.2"),sQuery(id+"F0.wireOp",EDGE,"E25.3"),sQuery(id+"F0.wireOp",EDGE,"E25.4"),sQuery(id+"F0.wireOp",EDGE,"E25.5"),sQuery(id+"F0.wireOp",EDGE,"E25.6"),sQuery(id+"F0.wireOp",EDGE,"E25.7")])],"isStart":false});
            extrude(context, id + "F17", {"entities" : qUnion([Q0, Q1, Q2, Q3]), "endBound" : BoundingType.UP_TO_SURFACE, "endBoundEntityFace" : qUnion([Q4]), "depth" : 25 * mm});
        }
    });
